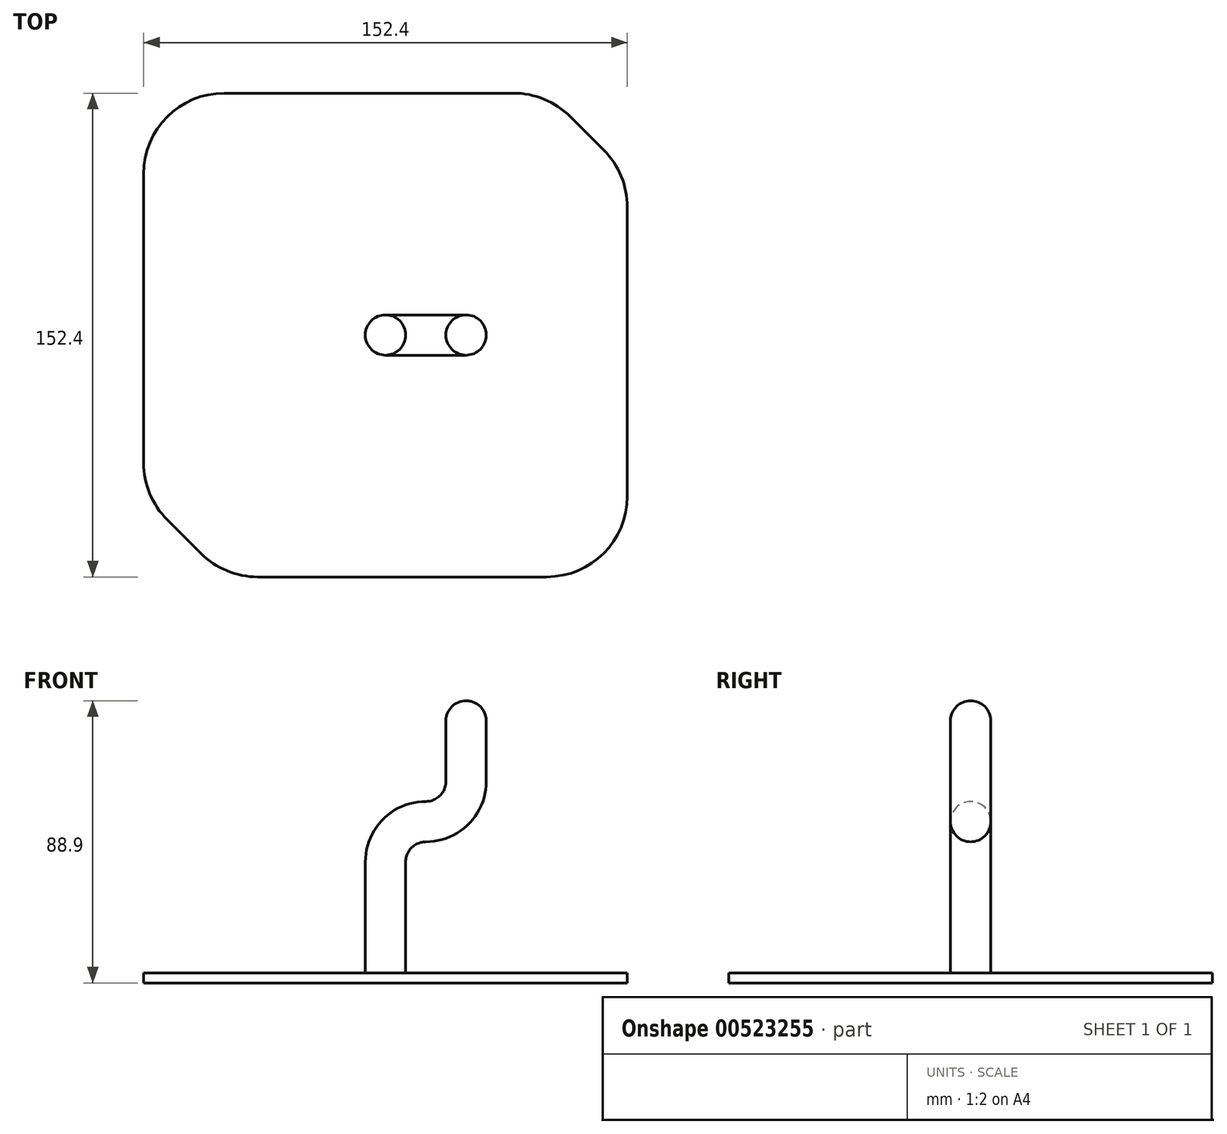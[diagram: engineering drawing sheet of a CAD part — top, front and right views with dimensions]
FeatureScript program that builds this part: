
annotation { "Feature Type Name" : "Feature", "Feature Type Description" : "" }
export const myFeature = defineFeature(function(context is Context, id is Id, definition is map)
    precondition{}
    {
        {
            var Q0;
            Q0=qCreatedBy(makeId("Top.planeOp"),FACE);
            var sketch = newSketch(context, id + "F0", { "sketchPlane" : qUnion([Q0])});
            skCircle(sketch, "E0", {"center": v(0, 0) * mm, "radius": 38.1 * mm});
            skPoint(sketch, "E1", {"position": v(38.1, 0) * mm});
            skSolve(sketch);
        }
        {
            var Q0;
            Q0=qCreatedBy(makeId("Front.planeOp"),FACE);
            var sketch = newSketch(context, id + "F1", { "sketchPlane" : qUnion([Q0])});
            skCircle(sketch, "E2", {"center": v(38.1, 0) * mm, "radius": 9.53 * mm});
            skSolve(sketch);
        }
        {
            var Q0;
            Q0=sQuery(id+"F1.wireOp",EDGE,"E2");
            var Q1;
            Q1=sQuery(id+"F0.wireOp",EDGE,"E0");
            revolve(context, id + "F2", {"bodyType" : ToolBodyType.SURFACE, "surfaceEntities" : qUnion([Q0]), "axis" : qUnion([Q1]), "revolveType" : RevolveType.FULL});
        }
        {
            var Q0;
            Q0=qCreatedBy(makeId("Top.planeOp"),FACE);
            var sketch = newSketch(context, id + "F3", { "sketchPlane" : qUnion([Q0])});
            skCircle(sketch, "E3", {"center": v(0, 0) * mm, "radius": 6.35 * mm});
            skSolve(sketch);
        }
        {
            var Q0;
            Q0=qCreatedBy(makeId("Front.planeOp"),FACE);
            var sketch = newSketch(context, id + "F4", { "sketchPlane" : qUnion([Q0])});
            skLineSegment(sketch, "E4", {"start": v(0, 0) * mm, "end": v(0, 25.4) * mm});
            skPoint(sketch, "E5.visualSharp", {"position": v(0, 4.02) * mm});
            skArc(sketch, "E6", {"start": v(12.7, 38.1) * mm, "mid": v(3.72, 34.38) * mm, "end": v(0, 25.4) * mm});
            skArc(sketch, "E7", {"start": v(12.7, 38.1) * mm, "mid": v(21.68, 41.82) * mm, "end": v(25.4, 50.8) * mm});
            skLineSegment(sketch, "E8", {"start": v(25.4, 50.8) * mm, "end": v(25.4, 76.2) * mm});
            skSolve(sketch);
        }
        {
            var Q0;
            Q0=makeQuery(id+"F3.imprint","IMPRINT",FACE,{"disambiguationData":[TD([[makeQuery(id+"F3.imprint","IMPRINT",EDGE,{"derivedFrom":sQuery(id+"F3.wireOp",EDGE,"E3")}),1.0]])]});
            var Q1;
            Q1=sQuery(id+"F4.wireOp",EDGE,"E7");
            var Q2;
            Q2=sQuery(id+"F4.wireOp",EDGE,"E4");
            var Q3;
            Q3=sQuery(id+"F4.wireOp",EDGE,"E6");
            var Q4;
            Q4=sQuery(id+"F4.wireOp",EDGE,"E8");
            sweep(context, id + "F5", {"profiles" : qUnion([Q0]), "path" : qUnion([Q1, Q2, Q3, Q4])});
        }
        {
            var Q0;
            Q0=qCreatedBy(makeId("Top.planeOp"),FACE);
            cPlane(context, id + "F6", {"entities" : qUnion([Q0]), "cplaneType" : CPlaneType.OFFSET, "offset" : 9.52 * mm, "oppositeDirection" : true, "width" : 152.4 * mm, "height" : 152.4 * mm});
        }
        {
            var Q0;
            Q0=qCreatedBy(id+"F6.planeOp",FACE);
            var sketch = newSketch(context, id + "F7", { "sketchPlane" : qUnion([Q0])});
            skLineSegment(sketch, "E9.bottom", {"start": v(76.2, 76.2) * mm, "end": v(-76.2, 76.2) * mm});
            skLineSegment(sketch, "E9.top", {"start": v(76.2, -76.2) * mm, "end": v(-76.2, -76.2) * mm});
            skLineSegment(sketch, "E9.left", {"start": v(76.2, 76.2) * mm, "end": v(76.2, -76.2) * mm});
            skLineSegment(sketch, "E9.right", {"start": v(-76.2, 76.2) * mm, "end": v(-76.2, -76.2) * mm});
            skPoint(sketch, "E9.middle", {"position": v(0, 0) * mm});
            skSolve(sketch);
        }
        {
            var Q0;
            Q0 = qSketchRegion(id + "F7", true);
            extrude(context, id + "F8", {"entities" : qUnion([Q0]), "oppositeDirection" : true, "depth" : 3.17 * mm, "offsetDistance" : 25.4 * mm});
        }
        {
            var Q0;
            Q0=makeQuery(id+"F5.opSweep","CAP_FACE",FACE,{"disambiguationData":[OSD([sQuery(id+"F3.wireOp",EDGE,"E3"),sQuery(id+"F4.wireOp",VERTEX,"E4.start")])],"isStart":true});
            extrude(context, id + "F9", {"entities" : qUnion([Q0]), "operationType" : NewBodyOperationType.ADD, "depth" : 9.52 * mm, "offsetDistance" : 25.4 * mm});
        }
        {
            var Q0;
            Q0=makeQuery(id+"F8.opExtrude","SWEPT_EDGE",EDGE,{"disambiguationData":[OSD([sQuery(id+"F7.wireOp",EDGE,"E9.top"),sQuery(id+"F7.wireOp",EDGE,"E9.left")])]});
            var Q1;
            Q1=makeQuery(id+"F8.opExtrude","SWEPT_EDGE",EDGE,{"disambiguationData":[OSD([sQuery(id+"F7.wireOp",EDGE,"E9.bottom"),sQuery(id+"F7.wireOp",EDGE,"E9.right")])]});
            fillet(context, id + "F10", {"entities" : qUnion([Q0, Q1]), "radius" : 25.4 * mm, "tangentPropagation" : true, "allowEdgeOverflow" : false});
        }
        {
            var Q0;
            Q0=makeQuery(id+"F8.opExtrude","SWEPT_EDGE",EDGE,{"disambiguationData":[OSD([sQuery(id+"F7.wireOp",EDGE,"E9.top"),sQuery(id+"F7.wireOp",EDGE,"E9.right")])]});
            var Q1;
            Q1=makeQuery(id+"F8.opExtrude","SWEPT_EDGE",EDGE,{"disambiguationData":[OSD([sQuery(id+"F7.wireOp",EDGE,"E9.bottom"),sQuery(id+"F7.wireOp",EDGE,"E9.left")])]});
            chamfer(context, id + "F11", {"entities" : qUnion([Q0, Q1]), "width" : 25.4 * mm, "tangentPropagation" : true});
        }
        {
            var Q0;
            {var subQ0=sQuery(id+"F7.wireOp",EDGE,"E9.right");Q0=makeQuery(id+"F11.opChamfer","BLEND_EDGE",EDGE,{"blendedFrom":[makeQuery(id+"F8.opExtrude","SWEPT_EDGE",EDGE,{"disambiguationData":[OSD([sQuery(id+"F7.wireOp",EDGE,"E9.top"),subQ0])]}),makeQuery(id+"F8.opExtrude","SWEPT_FACE",FACE,{"disambiguationData":[OSD([subQ0])]})],"blendedInto":[makeQuery(id+"F8.opExtrude","SWEPT_FACE",FACE,{"disambiguationData":[OSD([subQ0])]})]});}
            var Q1;
            {var subQ0=sQuery(id+"F7.wireOp",EDGE,"E9.top");Q1=makeQuery(id+"F11.opChamfer","BLEND_EDGE",EDGE,{"blendedFrom":[makeQuery(id+"F8.opExtrude","SWEPT_EDGE",EDGE,{"disambiguationData":[OSD([subQ0,sQuery(id+"F7.wireOp",EDGE,"E9.right")])]}),makeQuery(id+"F8.opExtrude","SWEPT_FACE",FACE,{"disambiguationData":[OSD([subQ0])]})],"blendedInto":[makeQuery(id+"F8.opExtrude","SWEPT_FACE",FACE,{"disambiguationData":[OSD([subQ0])]})]});}
            var Q2;
            {var subQ0=sQuery(id+"F7.wireOp",EDGE,"E9.left");Q2=makeQuery(id+"F11.opChamfer","BLEND_EDGE",EDGE,{"blendedFrom":[makeQuery(id+"F8.opExtrude","SWEPT_EDGE",EDGE,{"disambiguationData":[OSD([sQuery(id+"F7.wireOp",EDGE,"E9.bottom"),subQ0])]}),makeQuery(id+"F8.opExtrude","SWEPT_FACE",FACE,{"disambiguationData":[OSD([subQ0])]})],"blendedInto":[makeQuery(id+"F8.opExtrude","SWEPT_FACE",FACE,{"disambiguationData":[OSD([subQ0])]})]});}
            var Q3;
            {var subQ0=sQuery(id+"F7.wireOp",EDGE,"E9.bottom");Q3=makeQuery(id+"F11.opChamfer","BLEND_EDGE",EDGE,{"blendedFrom":[makeQuery(id+"F8.opExtrude","SWEPT_EDGE",EDGE,{"disambiguationData":[OSD([subQ0,sQuery(id+"F7.wireOp",EDGE,"E9.left")])]}),makeQuery(id+"F8.opExtrude","SWEPT_FACE",FACE,{"disambiguationData":[OSD([subQ0])]})],"blendedInto":[makeQuery(id+"F8.opExtrude","SWEPT_FACE",FACE,{"disambiguationData":[OSD([subQ0])]})]});}
            fillet(context, id + "F12", {"entities" : qUnion([Q0, Q1, Q2, Q3]), "radius" : 25.4 * mm, "tangentPropagation" : true, "allowEdgeOverflow" : false});
        }
        {
            var Q0;
            Q0=makeQuery(id+"F5.opSweep","CAP_EDGE",EDGE,{"disambiguationData":[OSD([sQuery(id+"F3.wireOp",EDGE,"E3"),sQuery(id+"F4.wireOp",VERTEX,"E8.end")])],"isStart":false});
            fillet(context, id + "F13", {"entities" : qUnion([Q0]), "radius" : 6.35 * mm, "tangentPropagation" : true, "allowEdgeOverflow" : false});
        }
    });
